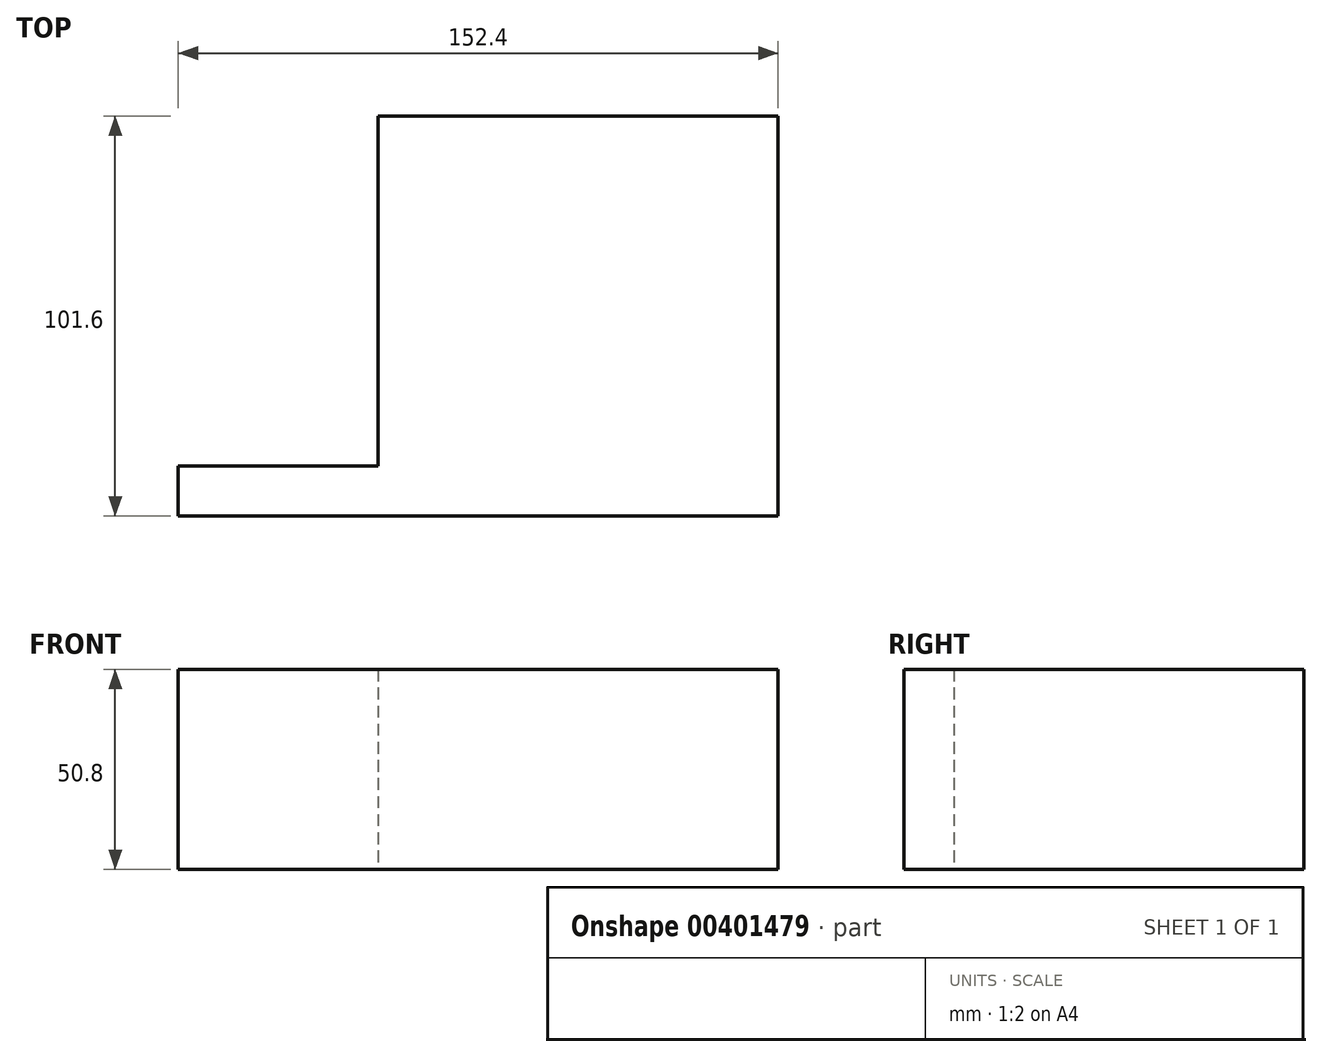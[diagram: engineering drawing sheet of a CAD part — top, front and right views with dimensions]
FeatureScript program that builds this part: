
annotation { "Feature Type Name" : "Feature", "Feature Type Description" : "" }
export const myFeature = defineFeature(function(context is Context, id is Id, definition is map)
    precondition{}
    {
        {
            var Q0;
            Q0=qCreatedBy(makeId("Top.planeOp"),FACE);
            var sketch = newSketch(context, id + "F0", { "sketchPlane" : qUnion([Q0])});
            skLineSegment(sketch, "E0.top", {"start": v(76.2, -50.8) * mm, "end": v(-76.2, -50.8) * mm});
            skLineSegment(sketch, "E0.left", {"start": v(76.2, 50.8) * mm, "end": v(76.2, -50.8) * mm});
            skPoint(sketch, "E0.middle", {"position": v(0, 0) * mm});
            skLineSegment(sketch, "E1", {"start": v(-76.2, -38.1) * mm, "end": v(-25.4, -38.1) * mm});
            skLineSegment(sketch, "E2", {"start": v(-25.4, -38.1) * mm, "end": v(-25.4, 50.8) * mm});
            skLineSegment(sketch, "E3", {"start": v(-25.4, 50.8) * mm, "end": v(76.2, 50.8) * mm});
            skLineSegment(sketch, "E4", {"start": v(-76.2, -38.1) * mm, "end": v(-76.2, -50.8) * mm});
            skSolve(sketch);
        }
        {
            var Q0;
            Q0 = qSketchRegion(id + "F0", true);
            extrude(context, id + "F1", {"entities" : qUnion([Q0]), "endBound" : BoundingType.SYMMETRIC, "depth" : 50.8 * mm});
        }
    });
